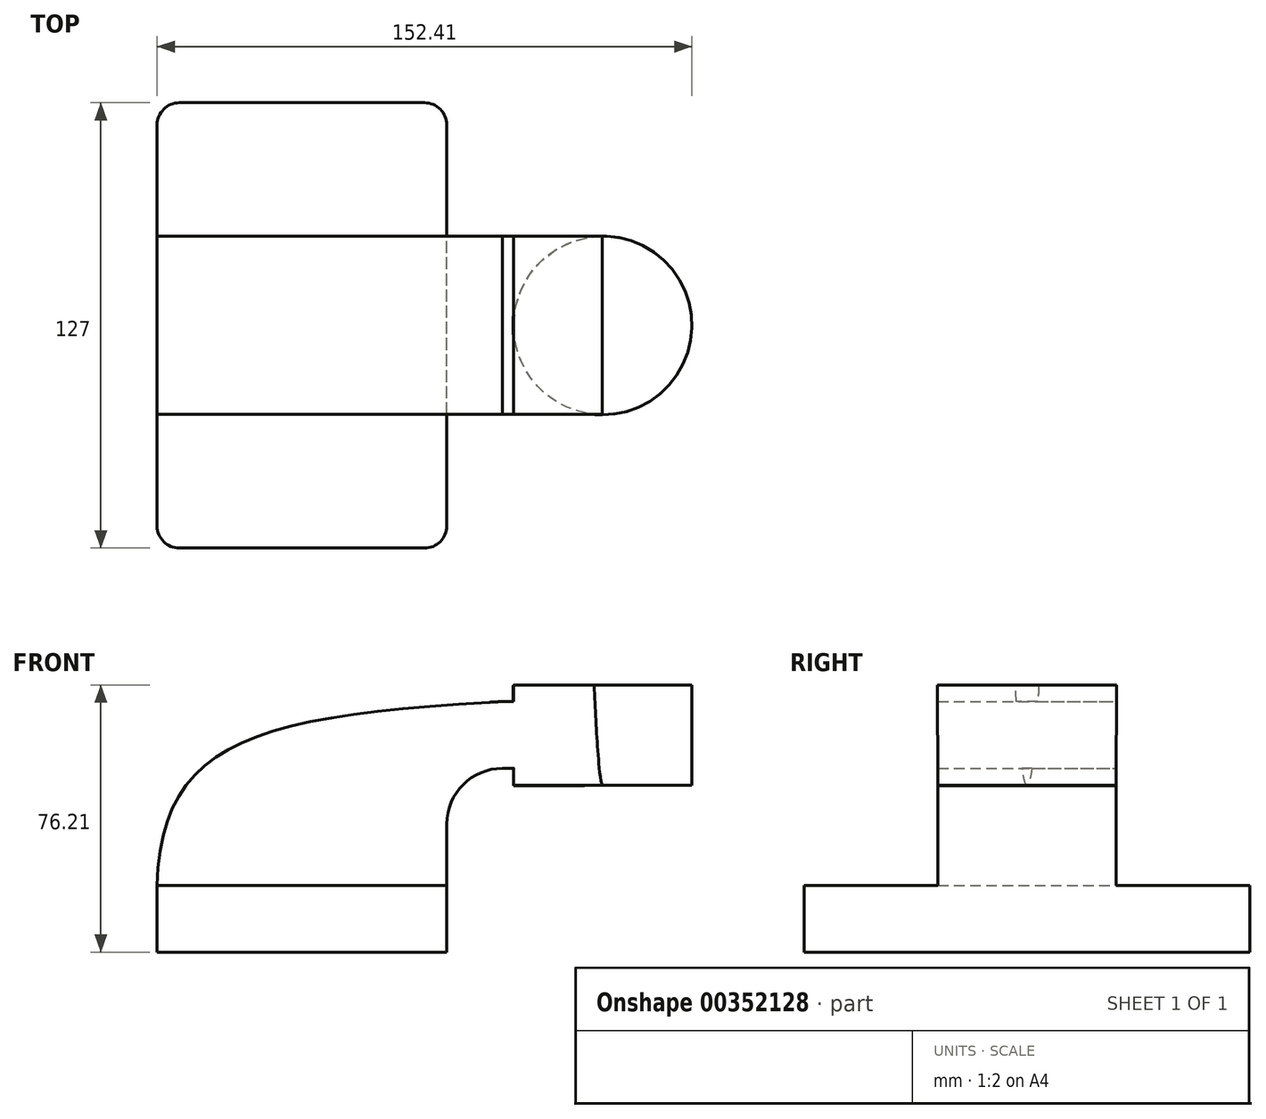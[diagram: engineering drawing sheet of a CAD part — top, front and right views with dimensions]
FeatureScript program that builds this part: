
annotation { "Feature Type Name" : "Feature", "Feature Type Description" : "" }
export const myFeature = defineFeature(function(context is Context, id is Id, definition is map)
    precondition{}
    {
        {
            var Q0;
            Q0=qCreatedBy(makeId("Front.planeOp"),FACE);
            var sketch = newSketch(context, id + "F0", { "sketchPlane" : qUnion([Q0])});
            skLineSegment(sketch, "E0.bottom", {"start": v(41.27, 9.53) * mm, "end": v(-41.28, 9.53) * mm});
            skLineSegment(sketch, "E0.top", {"start": v(41.28, -9.52) * mm, "end": v(-41.27, -9.52) * mm});
            skLineSegment(sketch, "E0.left", {"start": v(41.27, 9.53) * mm, "end": v(41.28, -9.52) * mm});
            skLineSegment(sketch, "E0.right", {"start": v(-41.28, 9.53) * mm, "end": v(-41.27, -9.52) * mm});
            skPoint(sketch, "E0.middle", {"position": v(0, 0) * mm});
            skLineSegment(sketch, "E1.bottom", {"start": v(111.12, 38.1) * mm, "end": v(60.33, 38.1) * mm});
            skLineSegment(sketch, "E1.top", {"start": v(111.12, 66.68) * mm, "end": v(60.32, 66.68) * mm});
            skLineSegment(sketch, "E1.left", {"start": v(111.12, 38.1) * mm, "end": v(111.12, 66.68) * mm});
            skLineSegment(sketch, "E1.right", {"start": v(60.33, 38.1) * mm, "end": v(60.33, 66.68) * mm});
            skPoint(sketch, "E1.middle", {"position": v(85.72, 52.39) * mm});
            skLineSegment(sketch, "E2", {"start": v(41.27, 9.53) * mm, "end": v(41.27, 27) * mm});
            skArc(sketch, "E3", {"start": v(41.27, 27) * mm, "mid": v(45.92, 38.23) * mm, "end": v(57.15, 42.88) * mm});
            skLineSegment(sketch, "E4", {"start": v(57.15, 42.88) * mm, "end": v(85.61, 42.88) * mm});
            skLineSegment(sketch, "E5.0", {"start": v(57.15, 61.93) * mm, "end": v(85.61, 61.93) * mm});
            skArc(sketch, "E5.1", {"start": v(22.22, 27) * mm, "mid": v(32.45, 51.7) * mm, "end": v(57.15, 61.93) * mm});
            skLineSegment(sketch, "E5.2", {"start": v(22.22, 9.53) * mm, "end": v(22.22, 27) * mm});
            skLineSegment(sketch, "E6", {"start": v(85.72, 38.1) * mm, "end": v(85.61, 66.68) * mm});
            skFitSpline(sketch, "E7", {"points": [v(-41.28, 9.53) * mm, v(57.15, 61.93) * mm], "startDerivative": vector(3.35, 122.53) * mm, "endDerivative": vector(213.12, 11.54) * mm});
            skSolve(sketch);
        }
        {
            var Q0;
            Q0=makeQuery(id+"F0.imprint","IMPRINT",FACE,{"disambiguationData":[TD([[makeQuery(id+"F0.imprint","IMPRINT",EDGE,{"derivedFrom":sQuery(id+"F0.wireOp",EDGE,"E0.top")}),-1.0]])]});
            extrude(context, id + "F1", {"entities" : qUnion([Q0]), "endBound" : BoundingType.SYMMETRIC, "depth" : 127 * mm});
        }
        {
            var Q0;
            {var subQ0=sQuery(id+"F0.wireOp",EDGE,"E7");var subQ1=sQuery(id+"F0.wireOp",EDGE,"E5.1");var subQ3=makeQuery(id+"F0.imprint","INTERSECT",VERTEX,{"derivedFrom":[subQ1,subQ0]});Q0=makeQuery(id+"F0.imprint","IMPRINT",FACE,{"disambiguationData":[TD([[makeQuery(id+"F0.imprint","IMPRINT",EDGE,{"disambiguationData":[TD([[subQ3,-1.0]])],"derivedFrom":subQ1}),-1.0]])]});}
            var Q1;
            Q1=makeQuery(id+"F0.imprint","IMPRINT",FACE,{"disambiguationData":[TD([[makeQuery(id+"F0.imprint","IMPRINT",EDGE,{"derivedFrom":sQuery(id+"F0.wireOp",EDGE,"E0.top")}),-1.0]])]});
            var Q2;
            {var subQ1=sQuery(id+"F0.wireOp",EDGE,"E2");Q2=makeQuery(id+"F0.imprint","IMPRINT",FACE,{"disambiguationData":[TD([[makeQuery(id+"F0.imprint","IMPRINT",EDGE,{"derivedFrom":subQ1}),1.0]])]});}
            var Q3;
            {var subQ6=sQuery(id+"F0.wireOp",EDGE,"E6");Q3=makeQuery(id+"F0.imprint","IMPRINT",FACE,{"disambiguationData":[TD([[makeQuery(id+"F0.imprint","IMPRINT",EDGE,{"derivedFrom":subQ6}),1.0]])]});}
            extrude(context, id + "F2", {"entities" : qUnion([Q0, Q1, Q2, Q3]), "operationType" : NewBodyOperationType.ADD, "endBound" : BoundingType.SYMMETRIC, "depth" : 50.8 * mm});
        }
        {
            var Q0;
            {var subQ0=sQuery(id+"F0.wireOp",EDGE,"E7");var subQ1=sQuery(id+"F0.wireOp",EDGE,"E5.1");var subQ3=makeQuery(id+"F0.imprint","INTERSECT",VERTEX,{"derivedFrom":[subQ1,subQ0]});Q0=makeQuery(id+"F0.imprint","IMPRINT",FACE,{"disambiguationData":[TD([[makeQuery(id+"F0.imprint","IMPRINT",EDGE,{"disambiguationData":[TD([[subQ3,-1.0]])],"derivedFrom":subQ1}),-1.0]])]});}
            var Q1;
            Q1=makeQuery(id+"F0.imprint","IMPRINT",FACE,{"disambiguationData":[TD([[makeQuery(id+"F0.imprint","IMPRINT",EDGE,{"derivedFrom":sQuery(id+"F0.wireOp",EDGE,"E0.top")}),-1.0]])]});
            var Q2;
            {var subQ3=sQuery(id+"F0.wireOp",EDGE,"E5.2");Q2=makeQuery(id+"F0.imprint","IMPRINT",FACE,{"disambiguationData":[TD([[makeQuery(id+"F0.imprint","IMPRINT",EDGE,{"derivedFrom":subQ3}),1.0]])]});}
            var Q3;
            {var subQ6=sQuery(id+"F0.wireOp",EDGE,"E6");Q3=makeQuery(id+"F0.imprint","IMPRINT",FACE,{"disambiguationData":[TD([[makeQuery(id+"F0.imprint","IMPRINT",EDGE,{"derivedFrom":subQ6}),1.0]])]});}
            var Q4;
            {var subQ1=sQuery(id+"F0.wireOp",EDGE,"E2");Q4=makeQuery(id+"F0.imprint","IMPRINT",FACE,{"disambiguationData":[TD([[makeQuery(id+"F0.imprint","IMPRINT",EDGE,{"derivedFrom":subQ1}),1.0]])]});}
            extrude(context, id + "F3", {"entities" : qUnion([Q0, Q1, Q2, Q3, Q4]), "operationType" : NewBodyOperationType.ADD, "endBound" : BoundingType.SYMMETRIC, "depth" : 15.88 * mm});
        }
        {
            var Q0;
            {var subQ0=sQuery(id+"F0.wireOp",EDGE,"E1.left");Q0=makeQuery(id+"F0.imprint","IMPRINT",FACE,{"disambiguationData":[TD([[makeQuery(id+"F0.imprint","IMPRINT",EDGE,{"derivedFrom":subQ0}),1.0]])]});}
            var Q1;
            Q1=sQuery(id+"F0.wireOp",EDGE,"E6");
            revolve(context, id + "F4", {"operationType" : NewBodyOperationType.ADD, "entities" : qUnion([Q0]), "axis" : qUnion([Q1]), "revolveType" : RevolveType.FULL});
        }
        {
            var Q0;
            Q0=makeQuery(id+"F1.opExtrude","CAP_EDGE",EDGE,{"disambiguationData":[OSD([sQuery(id+"F0.wireOp",EDGE,"E0.left")])],"isStart":false});
            var Q1;
            Q1=makeQuery(id+"F1.opExtrude","CAP_EDGE",EDGE,{"disambiguationData":[OSD([sQuery(id+"F0.wireOp",EDGE,"E0.left")])],"isStart":true});
            var Q2;
            Q2=makeQuery(id+"F1.opExtrude","CAP_EDGE",EDGE,{"disambiguationData":[OSD([sQuery(id+"F0.wireOp",EDGE,"E0.right")])],"isStart":true});
            var Q3;
            Q3=makeQuery(id+"F1.opExtrude","CAP_EDGE",EDGE,{"disambiguationData":[OSD([sQuery(id+"F0.wireOp",EDGE,"E0.right")])],"isStart":false});
            fillet(context, id + "F5", {"entities" : qUnion([Q0, Q1, Q2, Q3]), "radius" : 6.35 * mm, "tangentPropagation" : true, "allowEdgeOverflow" : false});
        }
    });
